# Revit family: KDW030006
name_source: partatom
category: Plumbing Fixtures
revit_build: Autodesk Revit 2015 (Build: 20140606_1530(x64)
units: mm (PartAtom-declared; Revit-internal decimal feet)

## types (1)
- KDW030006
    Additional features of the object = https://www.kaldewei.co.uk
    BIMobject category = Bath & Spas
    Brand url = http://www.kaldewei.com
    Color = https://www.kaldewei.co.uk
    ColourOptions = https://www.kaldewei.co.uk
    Configurator link = https://www.kaldewei.co.uk
    Description details = KALDEWEI international Worldwide partner for iconic bathroom solutions made of KALDEWEI steel enamel  KALDEWEI steel enamel delivers unique advantages that inspire excellence in bathroom design. Projects across the world, from upmarket hotels to private homes, capture the sophisticated aesthetic that recommends KALDEWEI as the partner of choice. As a leading international manufacturer of high-quality shower surfaces, bathtubs and washbasins made of superior steel enamel, KALDEWEI today is present in more than 80 countries.
    Design country = Germany
    DrainSize = 52 mm
    Durability = https://EN 14516
    Edition number = 1
    Finish = https://www.kaldewei.co.uk
    IFC Classification = Furnishing Element
    IfcExportAs = BATH
    IfcExportType = IfcSanitaryTerminalType
    Link towards a photo of the product = https://www.kaldewei.co.uk
    Manufacturer country = Germany
    ManufacturerCountry = GERMANY
    ManufacturerName = KALDEWEI
    Material = steel enamel
    Material main = Steel
    Material secondary = Enamel
    NBS Reference Code = 35-06-08
    NBS Reference Description = Baths
    Name = PUROSET WIDE LEFT
    Nominal height = 750 cm
    Nominal width = 1700 cm
    ObjectName = PUROSET WIDE LEFT 750x1700x380
    ObjectNorm = EN 14516 EU DECLARATION OF PERFORMANCE (https://www.kaldewei.de
    Polantis code = KDW030006
    Product Guid = bf5dd11d-01ea-4c3b-b159-cedebb76afac
    Product SKU = 668
    Product certification = https://www.kaldewei.co.uk
    Product data url = https://bimobject.com
    Product family = PURO
    Product group = Bathtub
    Product url = https://www.kaldewei.co.uk
    ProductInformation = Model No. 668: PURO SET WIDE combines bathing and showering in one tub in a completely new way. The centrally-positioned waste and overflow is not only an attractive design feature but allows for ample freedom of movement while showering. The reduced tub depth makes it easy to get in and out and reduces water consumption while bathing. The rim of the tub is flat and wide all the way round so taps and accessories can be placed anywhere – entirely in keeping with your personal preferences and the available space.
    QR code = http://bimobject.com
    SerialNumber = 668
    Shape = Rectangular baths
    Size = 750x1700x380
    Sound Insulation = DIN 4109:2016, VDI4100:2012
    Sustainability = https://kaldewei-fa.secure.footprint.net
    Technical data link = https://kaldewei.typo-live.web-factory.de
    Technical description = https://www.kaldewei.co.uk
    Type of accessories = https://www.kaldewei.co.uk
    Type of support framing = https://www.kaldewei.co.uk
    UNSPSC Code = 30181501
    UNSPSCCode = 30181500
    UNSPSCNames = Sanitary ware
    URL = https://www.kaldewei.com
    Uniclass 1.4 Code = L7211
    Uniclass 1.4 Description = Baths
    Uniclass 2.0 Code = PR-35-06-08
    Uniclass 2.0 Description = Baths
    Uniclass 2015 = Pr_40_20_06_08
    Version = 2
    WarrantyDurationParts = 30
    WarrantyDurationUnit = Year
    WarrantyStartDate = https://www.kaldewei.co.uk
    WaterSupplyOverflowAndWasteHolesOverflow = 52 mm
    WaterSupplyOverflowAndWasteHolesWaste = 52 mm
    Website link = https://www.kaldewei.co.uk
    Weight = 52
    Weight Net (Kg) = 52

## geometry (parser evidence)
native form markers: Sweep x15
no freeform markers — native parametric forms only
